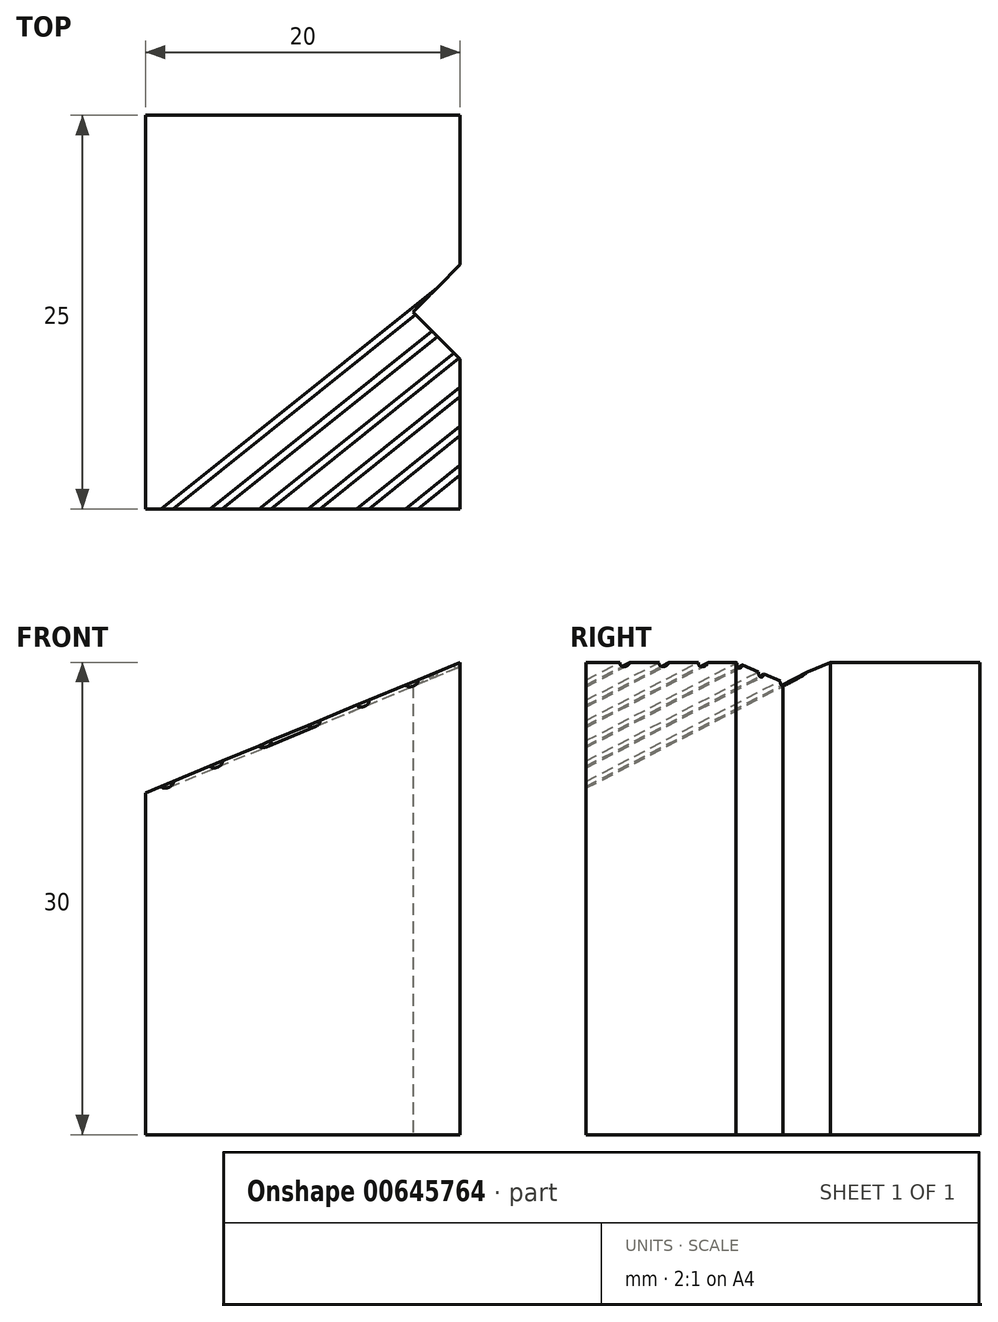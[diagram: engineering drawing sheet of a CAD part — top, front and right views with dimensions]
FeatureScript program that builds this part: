
annotation { "Feature Type Name" : "Feature", "Feature Type Description" : "" }
export const myFeature = defineFeature(function(context is Context, id is Id, definition is map)
    precondition{}
    {
        {
            var Q0;
            Q0=qCreatedBy(makeId("Front.planeOp"),FACE);
            var sketch = newSketch(context, id + "F0", { "sketchPlane" : qUnion([Q0])});
            skLineSegment(sketch, "E0", {"start": v(0, 0) * mm, "end": v(0, 30) * mm});
            skLineSegment(sketch, "E1", {"start": v(0, 30) * mm, "end": v(-20, 21.72) * mm});
            skLineSegment(sketch, "E2", {"start": v(-20, 21.72) * mm, "end": v(-20, 0) * mm});
            skLineSegment(sketch, "E3", {"start": v(-20, 0) * mm, "end": v(0, 0) * mm});
            skSolve(sketch);
        }
        {
            var Q0;
            Q0 = qSketchRegion(id + "F0", true);
            extrude(context, id + "F1", {"entities" : qUnion([Q0]), "depth" : 25 * mm, "offsetDistance" : 25 * mm});
        }
        {
            var Q0;
            Q0=makeQuery(id+"F1.opExtrude","SWEPT_FACE",FACE,{"disambiguationData":[OSD([sQuery(id+"F0.wireOp",EDGE,"E3")])]});
            var sketch = newSketch(context, id + "F2", { "sketchPlane" : qUnion([Q0])});
            skLineSegment(sketch, "E4", {"start": v(0, 12.5) * mm, "end": v(-20, 12.5) * mm, "construction": true});
            skLineSegment(sketch, "E5", {"start": v(0, 15.5) * mm, "end": v(-3, 12.5) * mm});
            skLineSegment(sketch, "E6.MirrorCS", {"start": v(0, 9.5) * mm, "end": v(-3, 12.5) * mm});
            skLineSegment(sketch, "E7", {"start": v(0, 15.5) * mm, "end": v(0, 9.5) * mm});
            skLineSegment(sketch, "E8", {"start": v(0, 0) * mm, "end": v(-65.5, 27.13) * mm, "construction": true});
            skPoint(sketch, "E9", {"position": v(-20, 8.28) * mm});
            skSolve(sketch);
        }
        {
            var Q0;
            Q0 = qSketchRegion(id + "F2", true);
            extrude(context, id + "F3", {"entities" : qUnion([Q0]), "operationType" : NewBodyOperationType.REMOVE, "endBound" : BoundingType.THROUGH_ALL, "oppositeDirection" : true, "depth" : 25 * mm, "offsetDistance" : 25 * mm});
        }
        {
            var Q0;
            Q0=makeQuery(id+"F1.opExtrude","SWEPT_FACE",FACE,{"disambiguationData":[OSD([sQuery(id+"F0.wireOp",EDGE,"E1")])]});
            var sketch = newSketch(context, id + "F4", { "sketchPlane" : qUnion([Q0])});
            skLineSegment(sketch, "E10", {"start": v(-10.17, -16) * mm, "end": v(11.48, 0) * mm, "construction": true});
            skSolve(sketch);
        }
        {
            var Q0;
            Q0=sQuery(id+"F4.wireOp",EDGE,"E10");
            var Q1;
            Q1=sQuery(id+"F4.wireOp",VERTEX,"E10.end");
            cPlane(context, id + "F5", {"entities" : qUnion([Q0, Q1]), "cplaneType" : CPlaneType.LINE_POINT, "offset" : 25 * mm, "width" : 150 * mm, "height" : 150 * mm});
        }
        {
            var Q0;
            Q0=qCreatedBy(id+"F5.planeOp",FACE);
            var sketch = newSketch(context, id + "F6", { "sketchPlane" : qUnion([Q0])});
            skPoint(sketch, "E11.0", {"position": v(-14.95, 27.72) * mm});
            skCircle(sketch, "E12", {"center": v(-14.95, 27.72) * mm, "radius": 0.25 * mm});
            skCircle(sketch, "E13.1.0.0", {"center": v(-16.95, 27.72) * mm, "radius": 0.25 * mm});
            skCircle(sketch, "E13.2.0.0", {"center": v(-18.95, 27.72) * mm, "radius": 0.25 * mm});
            skCircle(sketch, "E13.3.0.0", {"center": v(-20.95, 27.72) * mm, "radius": 0.25 * mm});
            skCircle(sketch, "E13.4.0.0", {"center": v(-22.95, 27.72) * mm, "radius": 0.25 * mm});
            skLineSegment(sketch, "E13.direction1", {"start": v(-14.95, 27.72) * mm, "end": v(-16.95, 27.72) * mm, "construction": true});
            skCircle(sketch, "E14.0.5.0", {"center": v(-24.95, 27.72) * mm, "radius": 0.25 * mm});
            skSolve(sketch);
        }
        {
            var Q0;
            Q0 = qSketchRegion(id + "F6", true);
            extrude(context, id + "F7", {"entities" : qUnion([Q0]), "operationType" : NewBodyOperationType.REMOVE, "endBound" : BoundingType.THROUGH_ALL, "oppositeDirection" : true, "depth" : 25 * mm, "offsetDistance" : 25 * mm});
        }
    });
